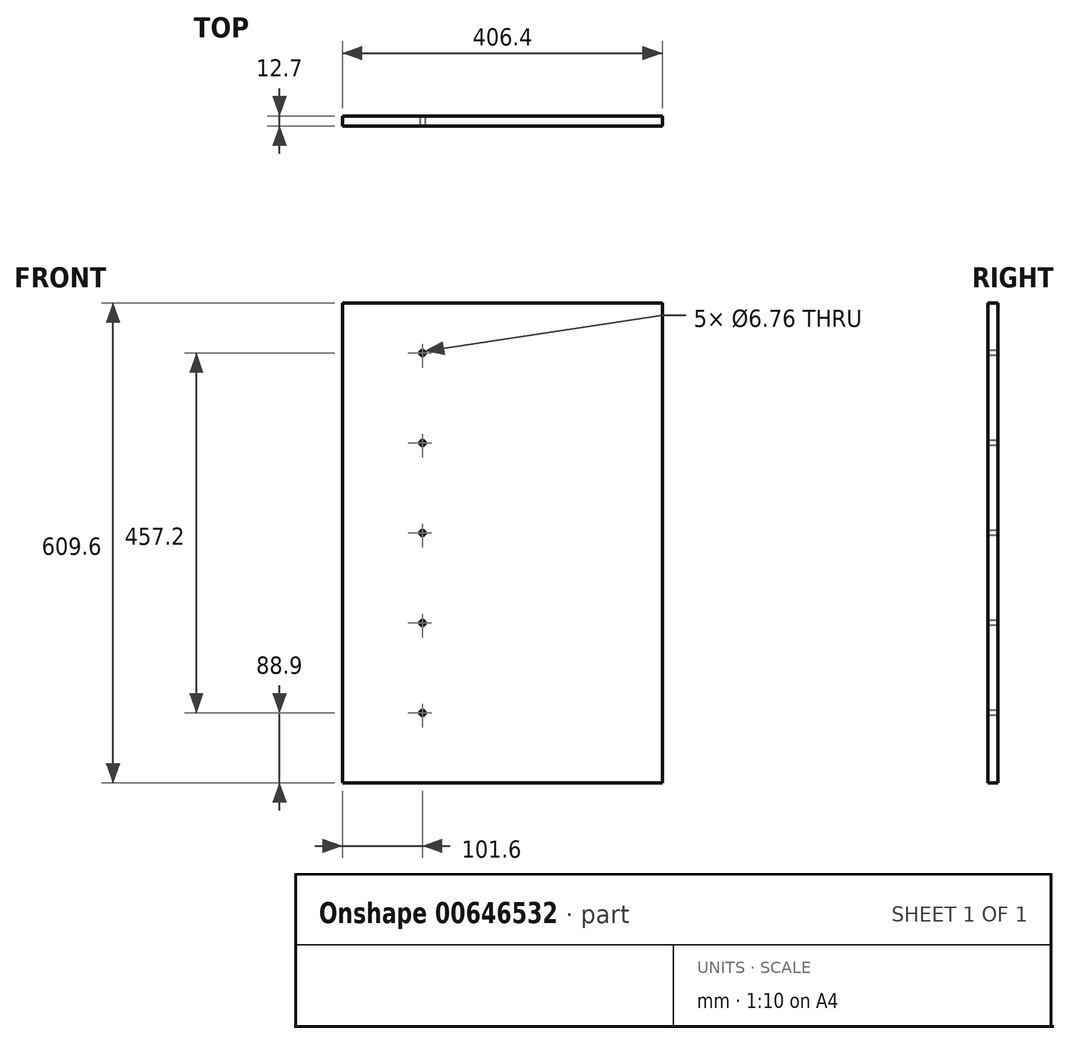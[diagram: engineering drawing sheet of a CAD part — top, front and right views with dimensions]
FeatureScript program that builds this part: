
annotation { "Feature Type Name" : "Feature", "Feature Type Description" : "" }
export const myFeature = defineFeature(function(context is Context, id is Id, definition is map)
    precondition{}
    {
        {
            var Q0;
            Q0=qCreatedBy(makeId("Front.planeOp"),FACE);
            var sketch = newSketch(context, id + "F0", { "sketchPlane" : qUnion([Q0])});
            skLineSegment(sketch, "E0.bottom", {"start": v(203.2, 304.8) * mm, "end": v(-203.2, 304.8) * mm});
            skLineSegment(sketch, "E0.top", {"start": v(203.2, -304.8) * mm, "end": v(-203.2, -304.8) * mm});
            skLineSegment(sketch, "E0.left", {"start": v(203.2, 304.8) * mm, "end": v(203.2, -304.8) * mm});
            skLineSegment(sketch, "E0.right", {"start": v(-203.2, 304.8) * mm, "end": v(-203.2, -304.8) * mm});
            skPoint(sketch, "E0.middle", {"position": v(0, 0) * mm});
            skSolve(sketch);
        }
        {
            var Q0;
            Q0 = qSketchRegion(id + "F0", true);
            extrude(context, id + "F1", {"entities" : qUnion([Q0]), "depth" : 12.7 * mm, "offsetDistance" : 25.4 * mm});
        }
        {
            var Q0;
            Q0=makeQuery(id+"F1.opExtrude","CAP_FACE",FACE,{"disambiguationData":[OSD([sQuery(id+"F0.wireOp",EDGE,"E0.bottom"),sQuery(id+"F0.wireOp",EDGE,"E0.top"),sQuery(id+"F0.wireOp",EDGE,"E0.left"),sQuery(id+"F0.wireOp",EDGE,"E0.right")])],"isStart":false});
            var sketch = newSketch(context, id + "F2", { "sketchPlane" : qUnion([Q0])});
            skPoint(sketch, "E1", {"position": v(-101.6, 241.3) * mm});
            skPoint(sketch, "E2", {"position": v(-101.6, 127) * mm});
            skPoint(sketch, "E3", {"position": v(-101.6, -101.6) * mm});
            skPoint(sketch, "E4", {"position": v(-101.6, -215.9) * mm});
            skPoint(sketch, "E5", {"position": v(-101.6, 12.7) * mm});
            skSolve(sketch);
        }
        {
            var Q0;
            Q0=sQuery(id+"F2.wireOp",VERTEX,"E1");
            var Q1;
            Q1=sQuery(id+"F2.wireOp",VERTEX,"E2");
            var Q2;
            Q2=sQuery(id+"F2.wireOp",VERTEX,"E5");
            var Q3;
            Q3=sQuery(id+"F2.wireOp",VERTEX,"E3");
            var Q4;
            Q4=sQuery(id+"F2.wireOp",VERTEX,"E4");
            var Q5;
            Q5=makeQuery(id+"F1.opExtrude","SWEPT_BODY",BODY,{"disambiguationData":[OSD([sQuery(id+"F0.wireOp",EDGE,"E0.bottom"),sQuery(id+"F0.wireOp",EDGE,"E0.top"),sQuery(id+"F0.wireOp",EDGE,"E0.left"),sQuery(id+"F0.wireOp",EDGE,"E0.right")])]});
            hole(context, id + "F3", {"style" : HoleStyle.SIMPLE, "endStyle" : HoleEndStyle.THROUGH, "standardTappedOrClearance" : lookupTablePath({ "standard" : "ANSI", "size" : "H (0.27)", "type" : "Drilled" }), "standardBlindInLast" : lookupTablePath({ "standard" : "ANSI", "size" : "H", "type" : "Drilled" }), "holeDiameter" : 6.76 * mm, "majorDiameter" : 6.35 * mm, "isTappedThrough" : true, "tappedDepth" : 12.7 * mm, "tapClearance" : 3, "startFromSketch" : true, "locations" : qUnion([Q0, Q1, Q2, Q3, Q4]), "scope" : qUnion([Q5])});
        }
    });
